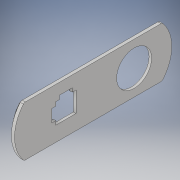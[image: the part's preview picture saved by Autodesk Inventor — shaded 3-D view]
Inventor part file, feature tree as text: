
AUTODESK INVENTOR PART (.ipt)
format: ipt  version: 2019 (Build 230136000, 136)  size: 444,416 bytes
history: native  units: in
note: dims shown in document units (in); Inventor stores cm internally (conversion verified against a paired STEP export)
features: extrude x13, sketch x13, projected_geometry x7, fillet x4, chamfer x1
ambient origin geometry x8: Origin, YZ Plane, XZ Plane, XY Plane, X Axis, Y Axis, Z Axis, Center Point
bodies: Solid1 (feature_tree), Solid2 (feature_tree)
feature tree (38):
  extrude  "Extrusion1"  Depth=1.5748in
  extrude  "Extrusion2"  Depth=0.0787in
  extrude  "Extrusion3"  Depth=0.5906in
  extrude  "Extrusion4"  Depth=0.1969in
  extrude  "Extrusion5"  Depth=0.1969in
  extrude  "Extrusion7"  Depth=0.1969in
  chamfer  "Chamfer1"  Distance=0.7874in
  extrude  "Extrusion8"  Depth=0.1181in TaperAngle=0.0deg
  extrude  "Extrusion9"  Depth=1.9685in TaperAngle=0.0deg
  extrude  "Extrusion10"  Depth=0.0787in TaperAngle=45.0deg
  extrude  "Extrusion11"  Depth=1.1811in
  extrude  "Extrusion12"  Depth=1.4173in TaperAngle=0.0deg
  extrude  "Extrusion13"  Depth=0.0197in
  extrude  "Extrusion14"  Depth=0.0472in
  fillet  "Fillet3"  Radius=0.0984in
  fillet  "Fillet4"  Radius=0.0984in
  fillet  "Fillet5"  Radius=0.7165in
  fillet  "Fillet6"  Radius=0.1181in
  sketch  "Sketch1"  dims[d0=4.3307in d1=1.5748in]
  sketch  "Sketch2"  dims[d2=0.0787in d3=0.0in d4=0.2756in]
  sketch  "Sketch3"  dims[d5=0.5906in d6=2.7559in]
  projected_geometry  "Projected Loop1"
  sketch  "Sketch4"  dims[d7=1.1811in d8=0.1969in]
  projected_geometry  "Projected Loop2"
  projected_geometry  "Projected Loop3"
  projected_geometry  "Projected Loop4"
  projected_geometry  "Projected Loop5"
  sketch  "Sketch5"  dims[d9=0.1969in d10=0.1969in]
  projected_geometry  "Projected Loop6"
  sketch  "Sketch7"  dims[d11=0.1969in d12=0.1969in]
  sketch  "Sketch9"  dims[d13=0.1969in d14=0.7874in d15=0.0in]
  sketch  "Sketch10"  dims[d16=0.3543in d17=0.0in d18=0.1181in d19=0.0in]
  sketch  "Sketch11"  dims[d20=0.0039in d21=1.9685in d22=0.0in]
  projected_geometry  "Projected Loop7"
  sketch  "Sketch12"  dims[d28=0.3543in d29=0.0in d31=0.3543in d32=0.0787in d33=45.0deg]
  sketch  "Sketch13"  dims[d34=1.1811in d35=1.1811in]
  sketch  "Sketch14"  dims[d36=0.0945in d37=1.4173in d38=0.0in]
  sketch  "Sketch15"  dims[d39=0.0787in d40=0.0in d41=0.0031in d42=0.0472in d43=0.0984in d44=0.0in d45=0.0984in d46=0.0in d47=0.7165in d48=0.1181in d50=0.3189in d51=0.6378in d52=0.6378in d53=0.1969in d54=0.1969in d55=0.1181in d56=1.9685in d57=0.0in d58=1.0984in d59=1.9685in d60=0.0in d61=1.9685in d62=0.0in d63=0.0787in d64=0.0197in d65=0.0197in d66=0.0197in]
